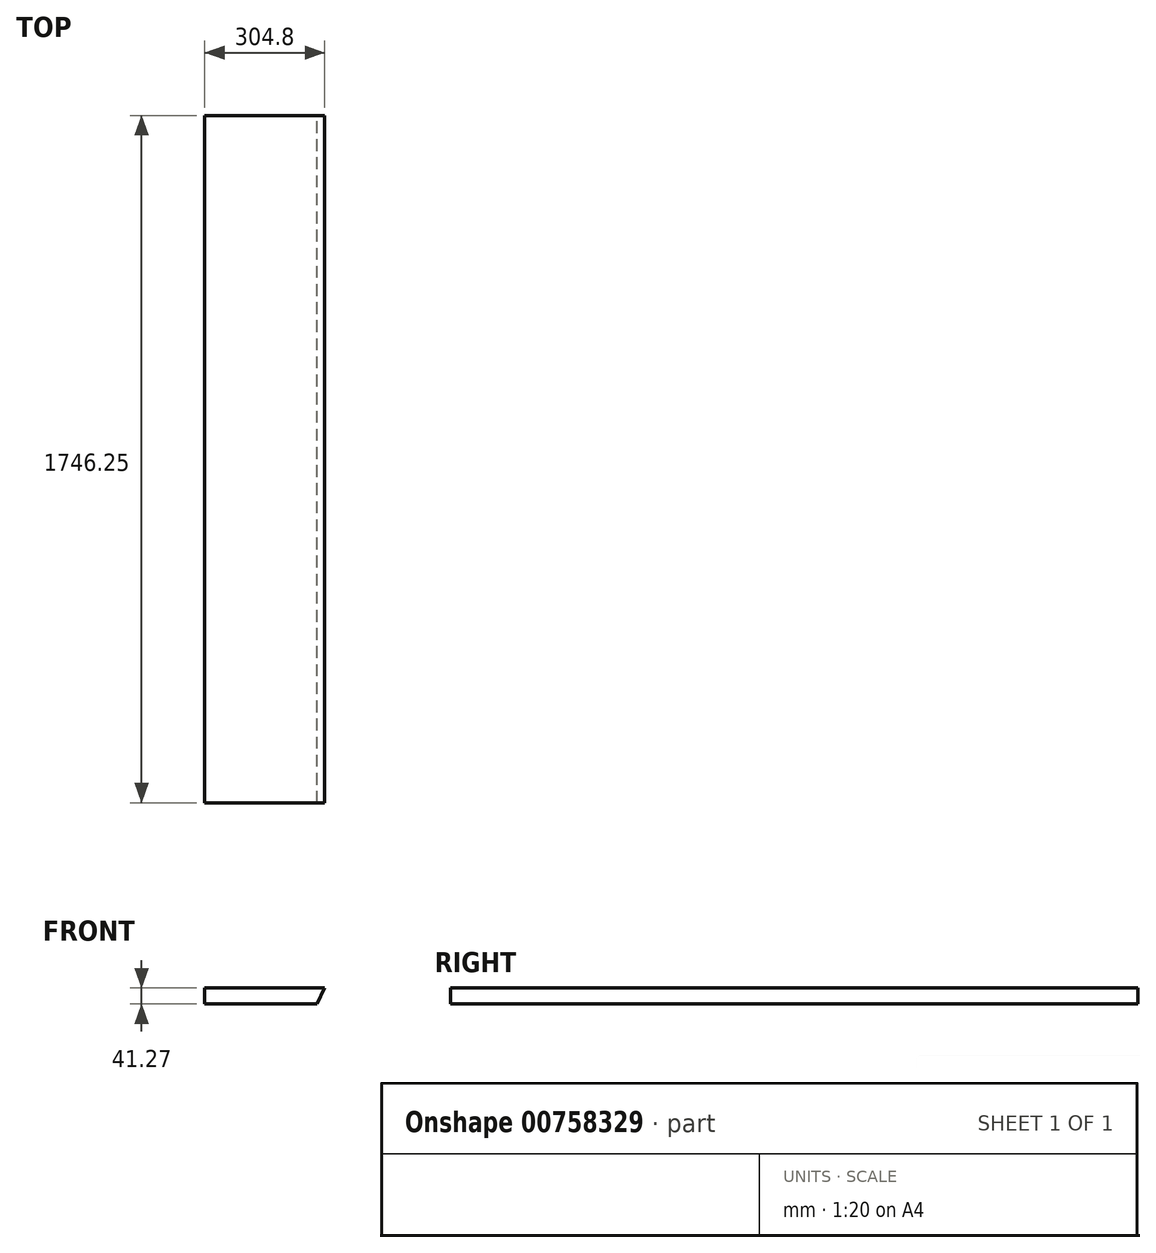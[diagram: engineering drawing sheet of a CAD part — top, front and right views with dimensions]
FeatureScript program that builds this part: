
annotation { "Feature Type Name" : "Feature", "Feature Type Description" : "" }
export const myFeature = defineFeature(function(context is Context, id is Id, definition is map)
    precondition{}
    {
        {
            var Q0;
            Q0=qCreatedBy(makeId("Front.planeOp"),FACE);
            var sketch = newSketch(context, id + "F0", { "sketchPlane" : qUnion([Q0])});
            skLineSegment(sketch, "E0", {"start": v(-160.64, 0) * mm, "end": v(-160.64, 41.28) * mm});
            skLineSegment(sketch, "E1", {"start": v(-160.64, 41.28) * mm, "end": v(144.16, 41.28) * mm});
            skLineSegment(sketch, "E2", {"start": v(-160.64, 0) * mm, "end": v(125.11, 0) * mm});
            skPoint(sketch, "E3.visualSharp", {"position": v(125.11, 41.28) * mm});
            skLineSegment(sketch, "E3.filletArc", {"start": v(144.16, 41.28) * mm, "end": v(144.16, 41.28) * mm});
            skLineSegment(sketch, "E4", {"start": v(144.16, 41.28) * mm, "end": v(125.11, 0) * mm});
            skSolve(sketch);
        }
        {
            var Q0;
            Q0=makeQuery(id+"F0.imprint","IMPRINT",FACE,{"disambiguationData":[TD([[makeQuery(id+"F0.imprint","IMPRINT",EDGE,{"derivedFrom":sQuery(id+"F0.wireOp",EDGE,"E0")}),-1.0]])]});
            extrude(context, id + "F1", {"entities" : qUnion([Q0]), "depth" : 1746.25 * mm, "offsetDistance" : 25.4 * mm});
        }
    });
